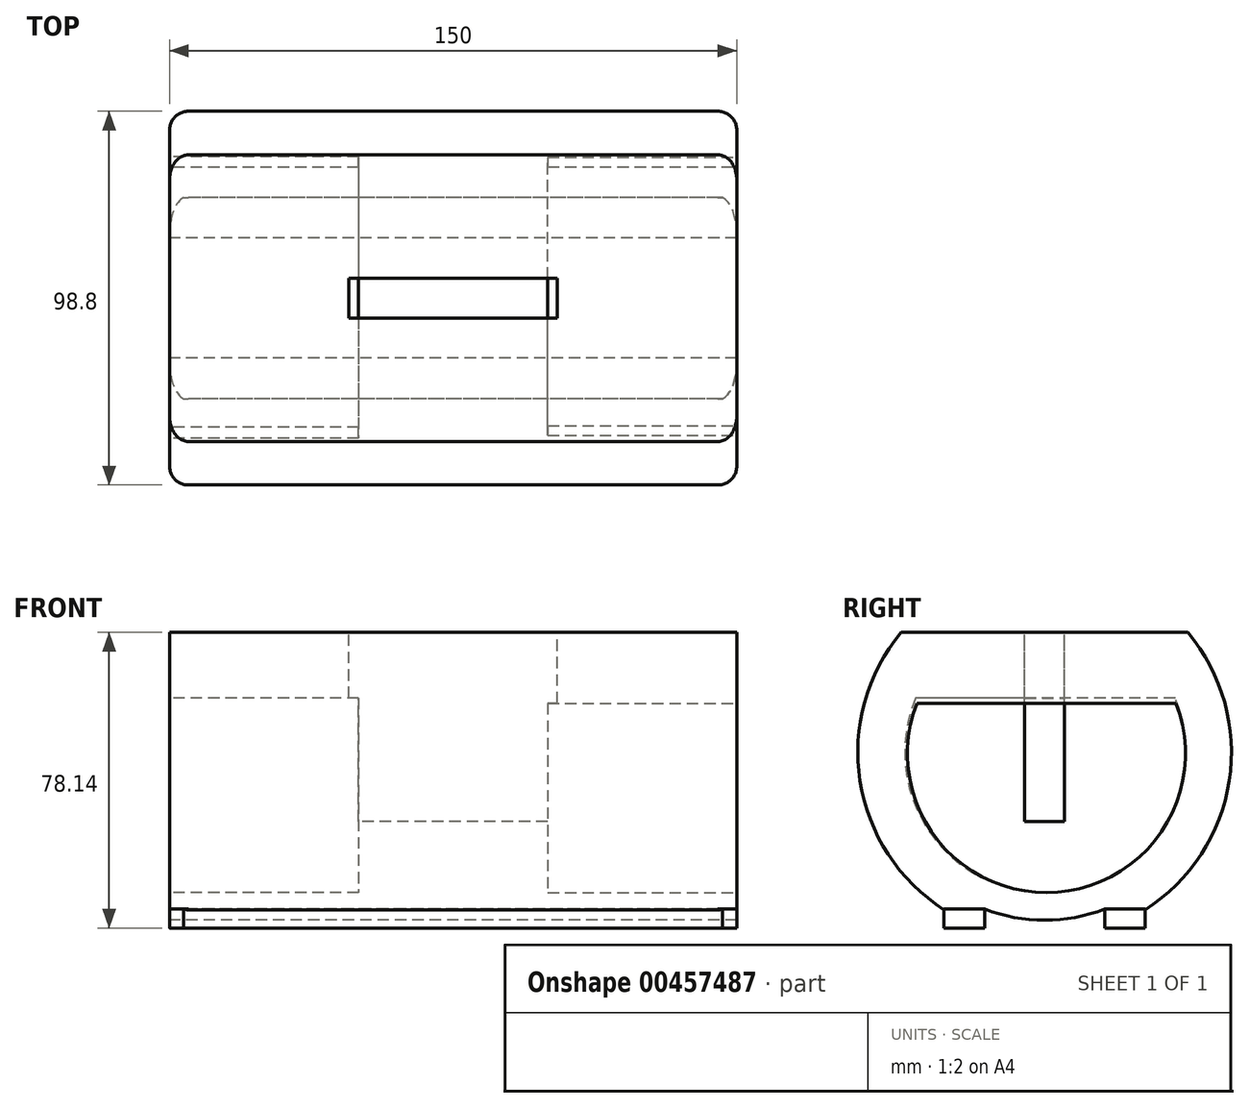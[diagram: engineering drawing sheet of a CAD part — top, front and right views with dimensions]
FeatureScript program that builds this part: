
annotation { "Feature Type Name" : "Feature", "Feature Type Description" : "" }
export const myFeature = defineFeature(function(context is Context, id is Id, definition is map)
    precondition{}
    {
        {
            var Q0;
            Q0=qCreatedBy(makeId("Right.planeOp"),FACE);
            var sketch = newSketch(context, id + "F0", { "sketchPlane" : qUnion([Q0])});
            skCircle(sketch, "E0", {"center": v(0, 0) * mm, "radius": 49.4 * mm});
            skSolve(sketch);
        }
        {
            var Q0;
            Q0=makeQuery(id+"F0.imprint","IMPRINT",FACE,{"disambiguationData":[TD([[makeQuery(id+"F0.imprint","IMPRINT",EDGE,{"derivedFrom":sQuery(id+"F0.wireOp",EDGE,"E0")}),1.0]])]});
            extrude(context, id + "F1", {"entities" : qUnion([Q0]), "depth" : 75 * mm});
        }
        {
            var Q0;
            Q0=makeQuery(id+"F1.opExtrude","CAP_FACE",FACE,{"disambiguationData":[OSD([sQuery(id+"F0.wireOp",EDGE,"E0")])],"isStart":true});
            var sketch = newSketch(context, id + "F2", { "sketchPlane" : qUnion([Q0])});
            skCircle(sketch, "E1", {"center": v(0, 0) * mm, "radius": 49.52 * mm});
            skSolve(sketch);
        }
        {
            var Q0;
            Q0=makeQuery(id+"F2.imprint","IMPRINT",FACE,{"disambiguationData":[TD([[makeQuery(id+"F2.imprint","IMPRINT",EDGE,{"derivedFrom":makeQuery(id+"F1.opExtrude","CAP_EDGE",EDGE,{"disambiguationData":[OSD([sQuery(id+"F0.wireOp",EDGE,"E0")])],"isStart":true})}),-1.0]])]});
            extrude(context, id + "F3", {"entities" : qUnion([Q0]), "operationType" : NewBodyOperationType.ADD, "depth" : 75 * mm});
        }
        {
            var Q0;
            Q0=makeQuery(id+"F3.opExtrude","CAP_FACE",FACE,{"disambiguationData":[OSD([sQuery(id+"F0.wireOp",EDGE,"E0")])],"isStart":false});
            var sketch = newSketch(context, id + "F4", { "sketchPlane" : qUnion([Q0])});
            skLineSegment(sketch, "E2", {"start": v(-37.9, 31.68) * mm, "end": v(37.9, 31.68) * mm});
            skSolve(sketch);
        }
        {
            var Q0;
            {var subQ0=sQuery(id+"F4.wireOp",EDGE,"E2");Q0=makeQuery(id+"F4.imprint","IMPRINT",FACE,{"disambiguationData":[TD([[makeQuery(id+"F4.imprint","IMPRINT",EDGE,{"derivedFrom":subQ0}),1.0]])]});}
            extrude(context, id + "F5", {"entities" : qUnion([Q0]), "operationType" : NewBodyOperationType.REMOVE, "oppositeDirection" : true, "depth" : 150 * mm});
        }
        {
            var Q0;
            Q0=makeQuery(id+"F5.boolean.opBoolean","COPY",FACE,{"derivedFrom":makeQuery(id+"F5.opExtrude","SWEPT_FACE",FACE,{"disambiguationData":[OSD([sQuery(id+"F4.wireOp",EDGE,"E2")])]})});
            var sketch = newSketch(context, id + "F6", { "sketchPlane" : qUnion([Q0])});
            skLineSegment(sketch, "E3.bottom", {"start": v(27.54, -5.24) * mm, "end": v(-27.54, -5.24) * mm});
            skLineSegment(sketch, "E3.top", {"start": v(27.54, 5.24) * mm, "end": v(-27.54, 5.24) * mm});
            skLineSegment(sketch, "E3.left", {"start": v(27.54, -5.24) * mm, "end": v(27.54, 5.24) * mm});
            skLineSegment(sketch, "E3.right", {"start": v(-27.54, -5.24) * mm, "end": v(-27.54, 5.24) * mm});
            skPoint(sketch, "E3.middle", {"position": v(0, 0) * mm});
            skSolve(sketch);
        }
        {
            var Q0;
            Q0=makeQuery(id+"F6.imprint","IMPRINT",FACE,{"disambiguationData":[TD([[makeQuery(id+"F6.imprint","IMPRINT",EDGE,{"derivedFrom":sQuery(id+"F6.wireOp",EDGE,"E3.bottom")}),-1.0]])]});
            extrude(context, id + "F7", {"entities" : qUnion([Q0]), "operationType" : NewBodyOperationType.REMOVE, "oppositeDirection" : true, "depth" : 50 * mm});
        }
        {
            var Q0;
            Q0=makeQuery(id+"F1.opExtrude","CAP_EDGE",EDGE,{"disambiguationData":[OSD([sQuery(id+"F0.wireOp",EDGE,"E0")])],"isStart":false});
            var Q1;
            Q1=makeQuery(id+"F5.boolean.opBoolean","COPY",EDGE,{"derivedFrom":makeQuery(id+"F5.opExtrude","CAP_EDGE",EDGE,{"disambiguationData":[OSD([sQuery(id+"F4.wireOp",EDGE,"E2")])],"isStart":false})});
            var Q2;
            {var subQ0=sQuery(id+"F4.wireOp",EDGE,"E2");var subQ1=sQuery(id+"F0.wireOp",EDGE,"E0");Q2=makeQuery(id+"F5.boolean.opBoolean","COPY",EDGE,{"derivedFrom":makeQuery(id+"F5.opExtrude","SWEPT_EDGE",EDGE,{"disambiguationData":[OSD([subQ1,subQ0]),TDD([makeQuery(id+"F4.imprint","INTERSECT",VERTEX,{"disambiguationData":[OD(0.0)],"derivedFrom":[makeQuery(id+"F3.opExtrude","CAP_EDGE",EDGE,{"disambiguationData":[OSD([subQ1])],"isStart":false}),subQ0]})])]})});}
            var Q3;
            {var subQ0=sQuery(id+"F4.wireOp",EDGE,"E2");var subQ1=sQuery(id+"F0.wireOp",EDGE,"E0");Q3=makeQuery(id+"F5.boolean.opBoolean","COPY",EDGE,{"derivedFrom":makeQuery(id+"F5.opExtrude","SWEPT_EDGE",EDGE,{"disambiguationData":[OSD([subQ1,subQ0]),TDD([makeQuery(id+"F4.imprint","INTERSECT",VERTEX,{"disambiguationData":[OD(1.0)],"derivedFrom":[makeQuery(id+"F3.opExtrude","CAP_EDGE",EDGE,{"disambiguationData":[OSD([subQ1])],"isStart":false}),subQ0]})])]})});}
            var Q4;
            Q4=makeQuery(id+"F3.opExtrude","CAP_EDGE",EDGE,{"disambiguationData":[OSD([sQuery(id+"F0.wireOp",EDGE,"E0")])],"isStart":false});
            var Q5;
            Q5=makeQuery(id+"F5.boolean.opBoolean","COPY",EDGE,{"derivedFrom":makeQuery(id+"F5.opExtrude","CAP_EDGE",EDGE,{"disambiguationData":[OSD([sQuery(id+"F4.wireOp",EDGE,"E2")])],"isStart":true})});
            fillet(context, id + "F8", {"entities" : qUnion([Q0, Q1, Q2, Q3, Q4, Q5]), "radius" : 5 * mm, "tangentPropagation" : true, "allowEdgeOverflow" : false});
        }
        {
            var Q0;
            Q0=makeQuery(id+"F1.opExtrude","CAP_FACE",FACE,{"disambiguationData":[OSD([sQuery(id+"F0.wireOp",EDGE,"E0")])],"isStart":false});
            var sketch = newSketch(context, id + "F9", { "sketchPlane" : qUnion([Q0])});
            skLineSegment(sketch, "E4", {"start": v(-33.75, 13) * mm, "end": v(31.81, 13) * mm});
            skLineSegment(sketch, "E5", {"start": v(31.81, 13) * mm, "end": v(34.72, 13) * mm});
            skArc(sketch, "E6", {"start": v(-33.75, 13) * mm, "mid": v(0.48, -37.1) * mm, "end": v(34.72, 13) * mm});
            skSolve(sketch);
        }
        {
            var Q0;
            Q0 = qSketchRegion(id + "F9", true);
            extrude(context, id + "F10", {"entities" : qUnion([Q0]), "operationType" : NewBodyOperationType.REMOVE, "oppositeDirection" : true, "depth" : 50 * mm});
        }
        {
            var Q0;
            Q0=makeQuery(id+"F3.opExtrude","CAP_FACE",FACE,{"disambiguationData":[OSD([sQuery(id+"F0.wireOp",EDGE,"E0")])],"isStart":false});
            var sketch = newSketch(context, id + "F11", { "sketchPlane" : qUnion([Q0])});
            skLineSegment(sketch, "E7", {"start": v(-34.53, 14.35) * mm, "end": v(31.23, 14.35) * mm});
            skLineSegment(sketch, "E8", {"start": v(31.23, 14.35) * mm, "end": v(34.14, 14.35) * mm});
            skArc(sketch, "E9", {"start": v(-34.53, 14.35) * mm, "mid": v(-0.2, -37.12) * mm, "end": v(34.14, 14.35) * mm});
            skSolve(sketch);
        }
        {
            var Q0;
            Q0 = qSketchRegion(id + "F11", true);
            extrude(context, id + "F12", {"entities" : qUnion([Q0]), "operationType" : NewBodyOperationType.REMOVE, "oppositeDirection" : true, "depth" : 50 * mm});
        }
        {
            var Q0;
            Q0=makeQuery(id+"F3.opExtrude","CAP_FACE",FACE,{"disambiguationData":[OSD([sQuery(id+"F0.wireOp",EDGE,"E0")])],"isStart":false});
            var sketch = newSketch(context, id + "F13", { "sketchPlane" : qUnion([Q0])});
            skLineSegment(sketch, "E10", {"start": v(-15.89, -41.46) * mm, "end": v(26.57, -41.46) * mm});
            skLineSegment(sketch, "E11", {"start": v(-15.89, -41.46) * mm, "end": v(-26.57, -41.46) * mm});
            skArc(sketch, "E12", {"start": v(-26.57, -41.46) * mm, "mid": v(0, -49.53) * mm, "end": v(26.57, -41.46) * mm});
            skSolve(sketch);
        }
        {
            var Q0;
            {var subQ5=sQuery(id+"F13.wireOp",EDGE,"E11");Q0=makeQuery(id+"F13.imprint","IMPRINT",FACE,{"disambiguationData":[TD([[makeQuery(id+"F13.imprint","IMPRINT",EDGE,{"derivedFrom":subQ5}),1.0]])]});}
            extrude(context, id + "F14", {"entities" : qUnion([Q0]), "operationType" : NewBodyOperationType.REMOVE, "oppositeDirection" : true, "depth" : 200 * mm});
        }
        {
            var Q0;
            Q0=makeQuery(id+"F14.boolean.opBoolean","COPY",FACE,{"derivedFrom":makeQuery(id+"F14.opExtrude","SWEPT_FACE",FACE,{"disambiguationData":[OSD([sQuery(id+"F13.wireOp",EDGE,"E10")])]})});
            var sketch = newSketch(context, id + "F15", { "sketchPlane" : qUnion([Q0])});
            skSolve(sketch);
        }
        {
            var Q0;
            Q0 = qSketchRegion(id + "F15", true);
            var Q1;
            {var subQ0=sQuery(id+"F13.wireOp",EDGE,"E10");Q1=makeQuery(id+"F15.imprint","IMPRINT",FACE,{"disambiguationData":[TD([[makeQuery(id+"F15.imprint","IMPRINT",EDGE,{"derivedFrom":makeQuery(id+"F14.boolean.opBoolean","COPY",EDGE,{"derivedFrom":makeQuery(id+"F14.opExtrude","SWEPT_EDGE",EDGE,{"disambiguationData":[OSD([subQ0,sQuery(id+"F13.wireOp",EDGE,"E12")])]})})}),1.0]])]});}
            var Q2;
            Q2=makeQuery(id+"F14.boolean.opBoolean","COPY",FACE,{"derivedFrom":makeQuery(id+"F14.opExtrude","SWEPT_FACE",FACE,{"disambiguationData":[OSD([sQuery(id+"F13.wireOp",EDGE,"E11")])]})});
            extrude(context, id + "F16", {"entities" : qUnion([Q0, Q1, Q2]), "operationType" : NewBodyOperationType.ADD, "depth" : 5 * mm});
        }
    });
